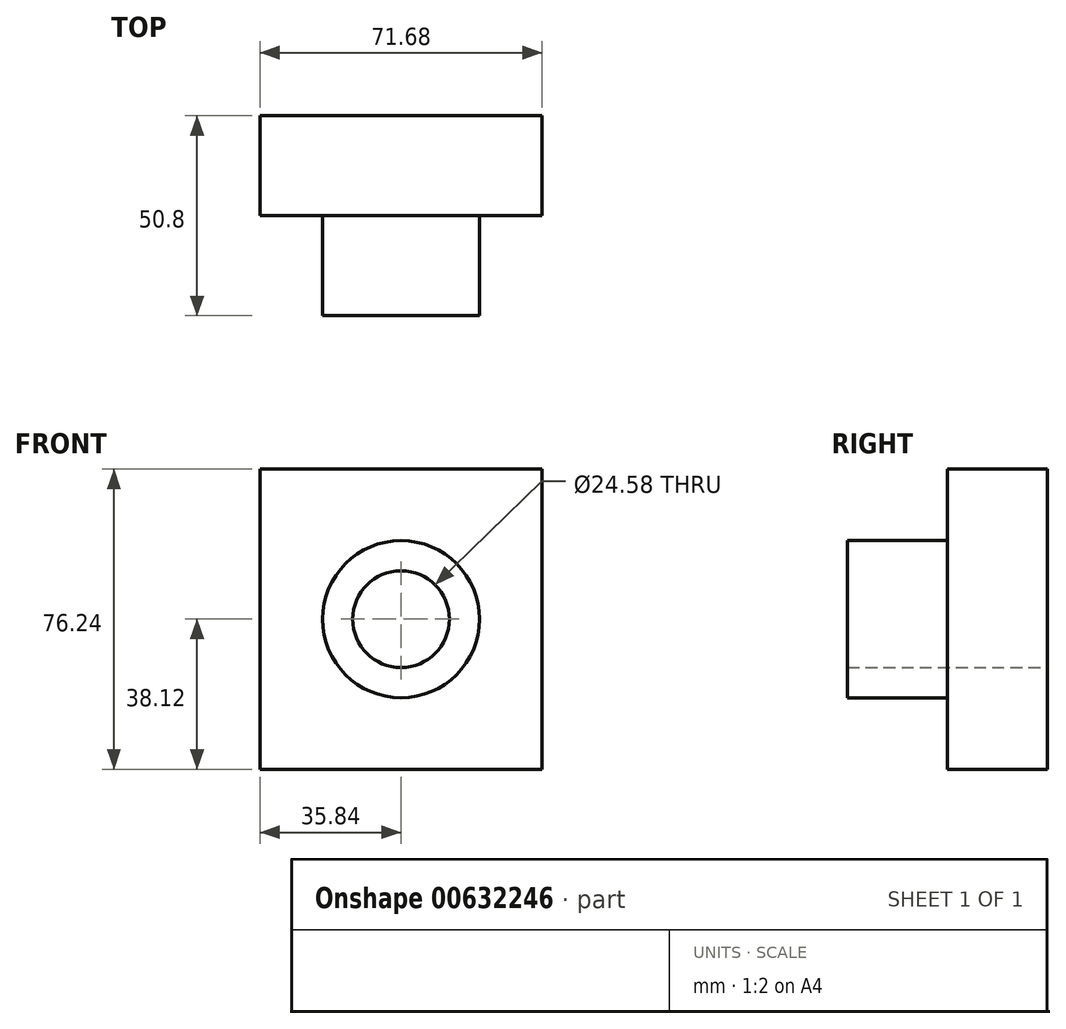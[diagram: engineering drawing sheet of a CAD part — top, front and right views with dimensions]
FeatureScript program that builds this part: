
annotation { "Feature Type Name" : "Feature", "Feature Type Description" : "" }
export const myFeature = defineFeature(function(context is Context, id is Id, definition is map)
    precondition{}
    {
        {
            var Q0;
            Q0=qCreatedBy(makeId("Front.planeOp"),FACE);
            var sketch = newSketch(context, id + "F0", { "sketchPlane" : qUnion([Q0])});
            skLineSegment(sketch, "E0.bottom", {"start": v(-35.84, 38.12) * mm, "end": v(35.84, 38.12) * mm});
            skLineSegment(sketch, "E0.top", {"start": v(-35.84, -38.12) * mm, "end": v(35.84, -38.12) * mm});
            skLineSegment(sketch, "E0.left", {"start": v(-35.84, 38.12) * mm, "end": v(-35.84, -38.12) * mm});
            skLineSegment(sketch, "E0.right", {"start": v(35.84, 38.12) * mm, "end": v(35.84, -38.12) * mm});
            skPoint(sketch, "E0.middle", {"position": v(0, 0) * mm});
            skSolve(sketch);
        }
        {
            var Q0;
            Q0 = qSketchRegion(id + "F0", true);
            extrude(context, id + "F1", {"entities" : qUnion([Q0]), "depth" : 25.4 * mm, "offsetDistance" : 25.4 * mm});
        }
        {
            var Q0;
            Q0=makeQuery(id+"F1.opExtrude","CAP_FACE",FACE,{"disambiguationData":[OSD([sQuery(id+"F0.wireOp",EDGE,"E0.bottom"),sQuery(id+"F0.wireOp",EDGE,"E0.top"),sQuery(id+"F0.wireOp",EDGE,"E0.left"),sQuery(id+"F0.wireOp",EDGE,"E0.right")])],"isStart":false});
            var sketch = newSketch(context, id + "F2", { "sketchPlane" : qUnion([Q0])});
            skCircle(sketch, "E1", {"center": v(0, 0) * mm, "radius": 19.95 * mm});
            skCircle(sketch, "E2", {"center": v(0, 0) * mm, "radius": 12.29 * mm});
            skSolve(sketch);
        }
        {
            var Q0;
            Q0=makeQuery(id+"F2.imprint","IMPRINT",FACE,{"disambiguationData":[TD([[makeQuery(id+"F2.imprint","IMPRINT",EDGE,{"derivedFrom":sQuery(id+"F2.wireOp",EDGE,"E1")}),1.0]])]});
            extrude(context, id + "F3", {"entities" : qUnion([Q0]), "operationType" : NewBodyOperationType.ADD, "depth" : 25.4 * mm, "offsetDistance" : 25.4 * mm});
        }
        {
            var Q0;
            Q0=makeQuery(id+"F3.boolean.opBoolean","SPLIT",FACE,{"disambiguationData":[TD([makeQuery(id+"F3.opExtrude","SWEPT_FACE",FACE,{"disambiguationData":[OSD([sQuery(id+"F2.wireOp",EDGE,"E2")])]})])],"derivedFrom":makeQuery(id+"F1.opExtrude","CAP_FACE",FACE,{"disambiguationData":[OSD([sQuery(id+"F0.wireOp",EDGE,"E0.bottom"),sQuery(id+"F0.wireOp",EDGE,"E0.top"),sQuery(id+"F0.wireOp",EDGE,"E0.left"),sQuery(id+"F0.wireOp",EDGE,"E0.right")])],"isStart":false})});
            extrude(context, id + "F4", {"entities" : qUnion([Q0]), "operationType" : NewBodyOperationType.REMOVE, "endBound" : BoundingType.THROUGH_ALL, "oppositeDirection" : true, "depth" : 25.4 * mm, "offsetDistance" : 25.4 * mm});
        }
    });
